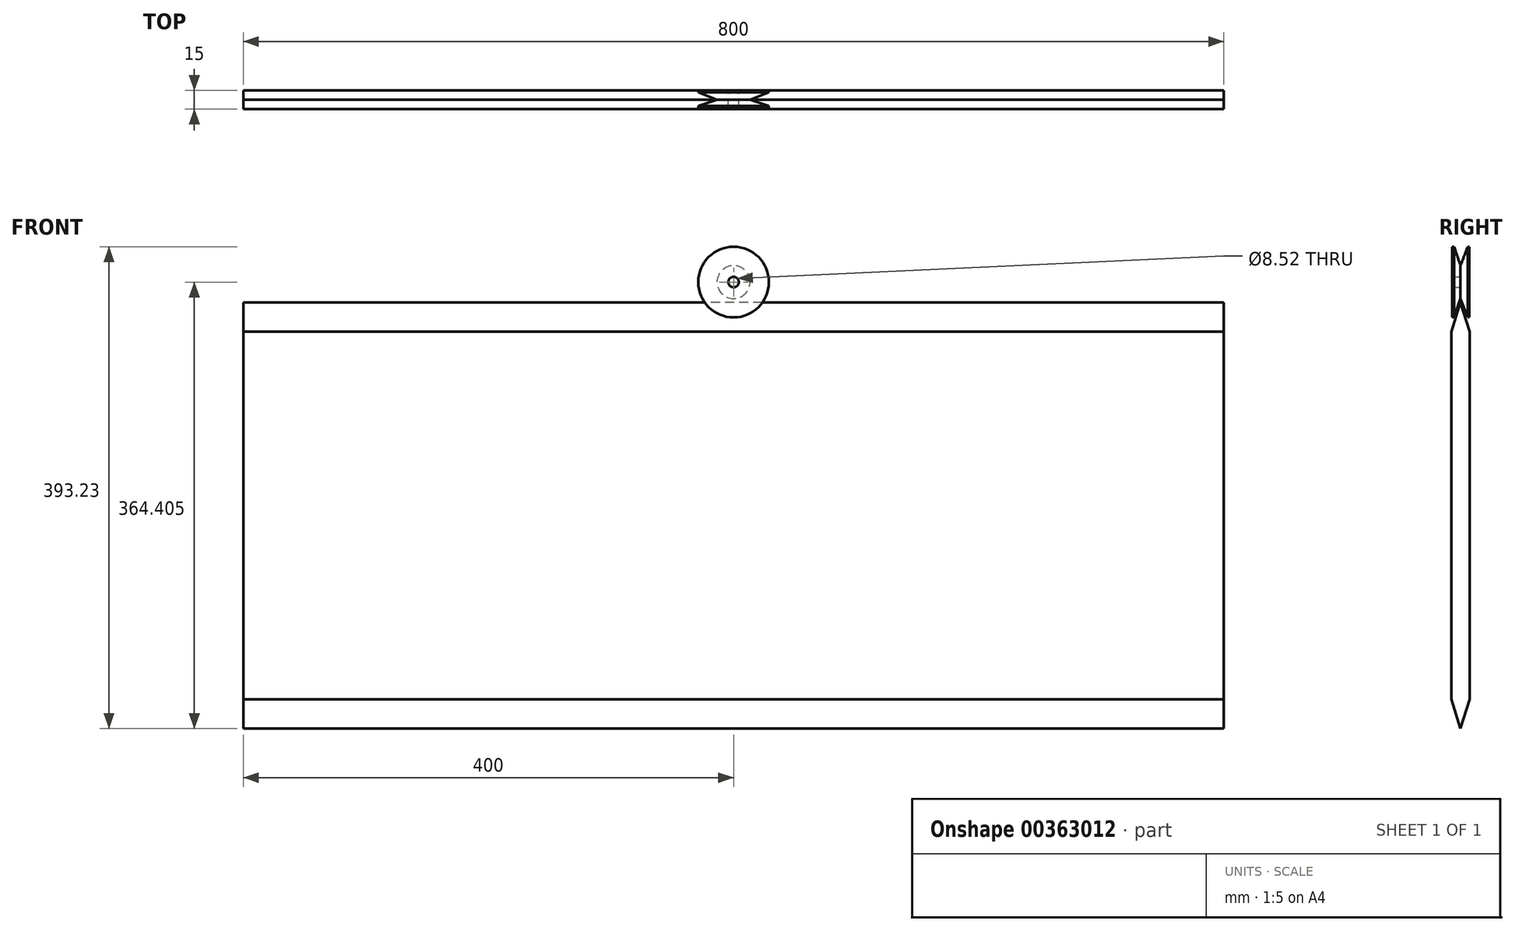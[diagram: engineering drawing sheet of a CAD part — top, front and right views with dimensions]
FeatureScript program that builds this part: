
annotation { "Feature Type Name" : "Feature", "Feature Type Description" : "" }
export const myFeature = defineFeature(function(context is Context, id is Id, definition is map)
    precondition{}
    {
        {
            var Q0;
            Q0=qCreatedBy(makeId("Right.planeOp"),FACE);
            var sketch = newSketch(context, id + "F0", { "sketchPlane" : qUnion([Q0])});
            skLineSegment(sketch, "E0.left", {"start": v(-7.5, 150) * mm, "end": v(-7.5, -150) * mm});
            skLineSegment(sketch, "E0.right", {"start": v(7.5, 150) * mm, "end": v(7.5, -150) * mm});
            skLineSegment(sketch, "E1", {"start": v(-7.5, 150) * mm, "end": v(0, 173.88) * mm});
            skLineSegment(sketch, "E2", {"start": v(0, 173.88) * mm, "end": v(7.5, 150) * mm});
            skLineSegment(sketch, "E3", {"start": v(-7.5, -150) * mm, "end": v(0, -173.88) * mm});
            skLineSegment(sketch, "E4", {"start": v(0, -173.88) * mm, "end": v(7.5, -150) * mm});
            skSolve(sketch);
        }
        {
            var Q0;
            Q0=makeQuery(id+"F0.imprint","IMPRINT",FACE,{"disambiguationData":[TD([[makeQuery(id+"F0.imprint","IMPRINT",EDGE,{"derivedFrom":sQuery(id+"F0.wireOp",EDGE,"E0.left")}),1.0]])]});
            extrude(context, id + "F1", {"entities" : qUnion([Q0]), "endBound" : BoundingType.SYMMETRIC, "depth" : 800 * mm});
        }
        {
            var Q0;
            Q0=qCreatedBy(makeId("Right.planeOp"),FACE);
            var sketch = newSketch(context, id + "F2", { "sketchPlane" : qUnion([Q0])});
            skLineSegment(sketch, "E5.bottom", {"start": v(-28.08, 190.53) * mm, "end": v(46.5, 190.53) * mm});
            skLineSegment(sketch, "E5.top", {"start": v(-28.08, 186.53) * mm, "end": v(46.5, 186.53) * mm});
            skLineSegment(sketch, "E5.left", {"start": v(-28.08, 190.53) * mm, "end": v(-28.08, 186.53) * mm});
            skLineSegment(sketch, "E5.right", {"start": v(46.5, 190.53) * mm, "end": v(46.5, 186.53) * mm});
            skSolve(sketch);
        }
        {
            var Q0;
            Q0=sQuery(id+"F2.wireOp",EDGE,"E5.top");
            var Q1;
            Q1=sQuery(id+"F2.wireOp",EDGE,"E5.left");
            var Q2;
            Q2=sQuery(id+"F2.wireOp",EDGE,"E5.right");
            var Q3;
            Q3=sQuery(id+"F2.wireOp",EDGE,"E5.bottom");
            revolve(context, id + "F3", {"bodyType" : ToolBodyType.SURFACE, "surfaceEntities" : qUnion([Q0, Q1, Q2]), "axis" : qUnion([Q3]), "revolveType" : RevolveType.FULL});
        }
        {
            var Q0;
            Q0=qCreatedBy(makeId("Right.planeOp"),FACE);
            var sketch = newSketch(context, id + "F4", { "sketchPlane" : qUnion([Q0])});
            skLineSegment(sketch, "E6", {"start": v(-5.08, 161.7) * mm, "end": v(0, 177.1) * mm});
            skLineSegment(sketch, "E7", {"start": v(0, 177.1) * mm, "end": v(5.9, 161.7) * mm});
            skLineSegment(sketch, "E8", {"start": v(5.9, 161.7) * mm, "end": v(7.23, 161.7) * mm});
            skLineSegment(sketch, "E9", {"start": v(7.23, 161.7) * mm, "end": v(6.54, 186.27) * mm});
            skLineSegment(sketch, "E10", {"start": v(6.54, 186.27) * mm, "end": v(-6.62, 186.27) * mm});
            skLineSegment(sketch, "E11", {"start": v(-6.62, 186.27) * mm, "end": v(-6.62, 161.7) * mm});
            skLineSegment(sketch, "E12", {"start": v(-6.62, 161.7) * mm, "end": v(-5.08, 161.7) * mm});
            skSolve(sketch);
        }
        {
            var Q0;
            Q0=makeQuery(id+"F4.imprint","IMPRINT",FACE,{"disambiguationData":[TD([[makeQuery(id+"F4.imprint","IMPRINT",EDGE,{"derivedFrom":sQuery(id+"F4.wireOp",EDGE,"E6")}),1.0]])]});
            var Q1;
            Q1=makeQuery(id+"F3.opRevolve","SWEPT_FACE",FACE,{"disambiguationData":[OSD([sQuery(id+"F2.wireOp",EDGE,"E5.top")])]});
            revolve(context, id + "F5", {"entities" : qUnion([Q0]), "axis" : qUnion([Q1]), "revolveType" : RevolveType.FULL});
        }
    });
